# Revit family: Drinking_Fountain-Wall_Mounted-Murdock_Mfg-M-OBA_Series
name_source: partatom
category: Plumbing Fixtures
units: mm (PartAtom-declared; Revit-internal decimal feet)

## family parameters
Cut with Voids When Loaded = No
Host = Face
OmniClass Number = 23.65.70.14.11
OmniClass Title = Drinking Fountains/Coolers
Part Type = Normal
Room Calculation Point = No
Round Connector Dimension = Use Diameter
Shared = Yes

## types (4) — shared parameters
ADA Compliant = Yes
Activation = Pushbutton and Sensor Operation
Assembly Code = D2010800
BAT Battery Operated = No
CSC - Concealed support carrier = No
CW Connection = Yes
CWFU = 1.5
Cold Water Connection Diameter = 1/2"
Default Elevation = 0"
Description = Barrier-Free Outdoor Wall Mount Bottle Filler
Diameter = 11"
FRA1 - Freeze resistant valve = No
Flow Rate = 1.0 GPM
HW Connection = No
Height = 22 3/4"
IAPMO Compliance = ANSI A117.1, Public Law 111-380 (NO-LEAD), CHSC 116875 and NSF/ANSI 61, Section 9
Installation Instruction Link = https://www.murdockmfg.com
Installation Type = Wall Mounted
MO Bottle filler operated by pushbutton only = No
Manufacturer = Murdock Mfg
Pressure Range = 30 to 100 psi
Price = Prices may vary. Please consult Manufacturer Representative for most up-to-date price list.
Product Documentation Link = https://www.murdockmfg.com
Product Page URL = https://www.murdockmfg.com
URL = https://www.murdockmfg.com
Vent Connection = No
WFU = 2
Warranty Information = 1 Year Limited Warranty
Waste Connection = Yes
Waste Connection Diameter = 1 1/4"
Waste Connection Height = 26 5/8"
Water Pressure = 20-105 PSIG
cUPC Compliant = Yes
zero-valued in all types: HWFU

## per-type parameters (varying)
| type | Finish | Material |
| M-OBA4 | Stainless Steel-Murdock-Satin | Stainless Steel-Murdock-Satin |
| M-OBA5 | Stainless Steel-Murdock-Green Powder Coated | Stainless Steel-Murdock-Green Powder Coated |
| M-OBA6 | Stainless Steel-Murdock-Red Powder Coated | Stainless Steel-Murdock-Red Powder Coated |
| M-OBA7 | Stainless Steel-Murdock-Blue Powder Coated | Stainless Steel-Murdock-Blue Powder Coated |

note: column(s) folded — value = type name in every type: Model

## geometry (parser evidence)
native form markers: Sweep x2
no freeform markers — native parametric forms only
